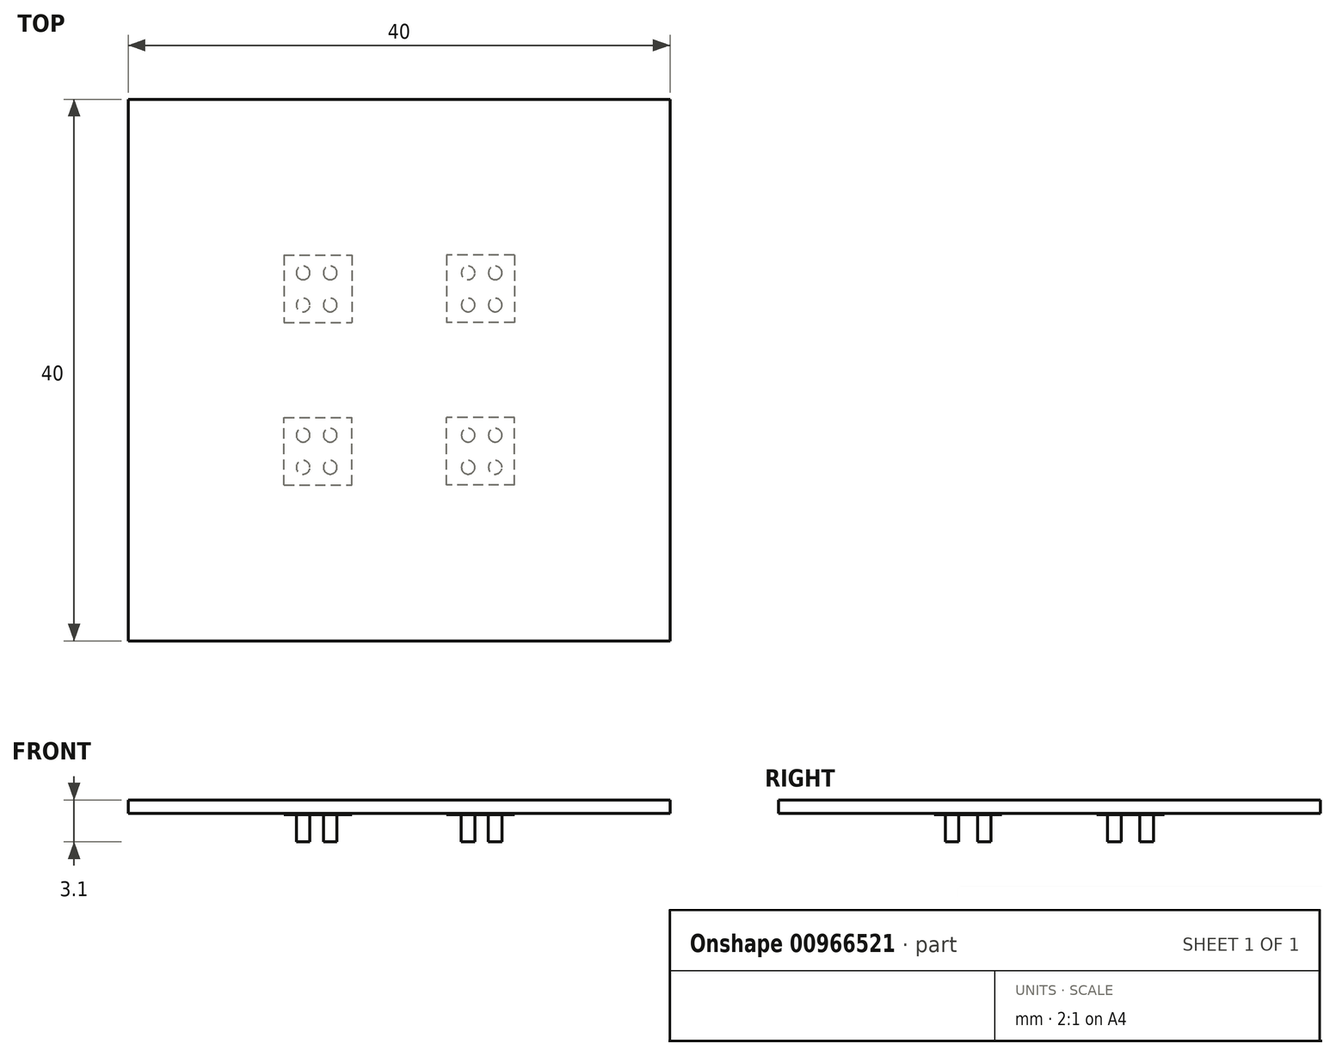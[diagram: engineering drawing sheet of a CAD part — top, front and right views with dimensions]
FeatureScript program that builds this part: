
annotation { "Feature Type Name" : "Feature", "Feature Type Description" : "" }
export const myFeature = defineFeature(function(context is Context, id is Id, definition is map)
    precondition{}
    {
        {
            var Q0;
            Q0=qCreatedBy(makeId("Top.planeOp"),FACE);
            var sketch = newSketch(context, id + "F0", { "sketchPlane" : qUnion([Q0])});
            skLineSegment(sketch, "E0.bottom", {"start": v(20, 20) * mm, "end": v(-20, 20) * mm});
            skLineSegment(sketch, "E0.top", {"start": v(20, -20) * mm, "end": v(-20, -20) * mm});
            skLineSegment(sketch, "E0.left", {"start": v(20, 20) * mm, "end": v(20, -20) * mm});
            skLineSegment(sketch, "E0.right", {"start": v(-20, 20) * mm, "end": v(-20, -20) * mm});
            skPoint(sketch, "E0.middle", {"position": v(0, 0) * mm});
            skLineSegment(sketch, "E1.bottom", {"start": v(-8.5, 8.5) * mm, "end": v(-3.5, 8.5) * mm});
            skLineSegment(sketch, "E1.top", {"start": v(-8.5, 3.5) * mm, "end": v(-3.5, 3.5) * mm});
            skLineSegment(sketch, "E1.left", {"start": v(-8.5, 8.5) * mm, "end": v(-8.5, 3.5) * mm});
            skLineSegment(sketch, "E1.right", {"start": v(-3.5, 8.5) * mm, "end": v(-3.5, 3.5) * mm});
            skLineSegment(sketch, "E2.MirrorCS", {"start": v(8.5, 8.5) * mm, "end": v(3.5, 8.5) * mm});
            skLineSegment(sketch, "E3.MirrorCS", {"start": v(8.5, 3.5) * mm, "end": v(3.5, 3.5) * mm});
            skLineSegment(sketch, "E4.MirrorCS", {"start": v(8.5, 8.5) * mm, "end": v(8.5, 3.5) * mm});
            skLineSegment(sketch, "E5.MirrorCS", {"start": v(3.5, 8.5) * mm, "end": v(3.5, 3.5) * mm});
            skLineSegment(sketch, "E6.MirrorCS", {"start": v(-8.5, -3.5) * mm, "end": v(-3.5, -3.5) * mm});
            skLineSegment(sketch, "E7.MirrorCS", {"start": v(-8.5, -8.5) * mm, "end": v(-3.5, -8.5) * mm});
            skLineSegment(sketch, "E8.MirrorCS", {"start": v(3.5, -8.5) * mm, "end": v(3.5, -3.5) * mm});
            skLineSegment(sketch, "E9.MirrorCS", {"start": v(-8.5, -8.5) * mm, "end": v(-8.5, -3.5) * mm});
            skLineSegment(sketch, "E10.MirrorCS", {"start": v(8.5, -8.5) * mm, "end": v(3.5, -8.5) * mm});
            skLineSegment(sketch, "E11.MirrorCS", {"start": v(8.5, -8.5) * mm, "end": v(8.5, -3.5) * mm});
            skLineSegment(sketch, "E12.MirrorCS", {"start": v(8.5, -3.5) * mm, "end": v(3.5, -3.5) * mm});
            skLineSegment(sketch, "E13.MirrorCS", {"start": v(-3.5, -8.5) * mm, "end": v(-3.5, -3.5) * mm});
            skSolve(sketch);
        }
        {
            var Q0;
            Q0=makeQuery(id+"F0.imprint","IMPRINT",FACE,{"disambiguationData":[TD([[makeQuery(id+"F0.imprint","IMPRINT",EDGE,{"derivedFrom":sQuery(id+"F0.wireOp",EDGE,"E1.bottom")}),-1.0]])]});
            var Q1;
            Q1=makeQuery(id+"F0.imprint","IMPRINT",FACE,{"disambiguationData":[TD([[makeQuery(id+"F0.imprint","IMPRINT",EDGE,{"derivedFrom":sQuery(id+"F0.wireOp",EDGE,"E2.MirrorCS")}),1.0]])]});
            var Q2;
            Q2=makeQuery(id+"F0.imprint","IMPRINT",FACE,{"disambiguationData":[TD([[makeQuery(id+"F0.imprint","IMPRINT",EDGE,{"derivedFrom":sQuery(id+"F0.wireOp",EDGE,"E8.MirrorCS")}),-1.0]])]});
            var Q3;
            Q3=makeQuery(id+"F0.imprint","IMPRINT",FACE,{"disambiguationData":[TD([[makeQuery(id+"F0.imprint","IMPRINT",EDGE,{"derivedFrom":sQuery(id+"F0.wireOp",EDGE,"E6.MirrorCS")}),-1.0]])]});
            extrude(context, id + "F1", {"entities" : qUnion([Q0, Q1, Q2, Q3]), "oppositeDirection" : true, "depth" : 0.1 * mm, "offsetDistance" : 25 * mm});
        }
        {
            var Q0;
            Q0=qCreatedBy(makeId("Top.planeOp"),FACE);
            var sketch = newSketch(context, id + "F2", { "sketchPlane" : qUnion([Q0])});
            skLineSegment(sketch, "E14.bottom", {"start": v(20, 20) * mm, "end": v(-20, 20) * mm});
            skLineSegment(sketch, "E14.top", {"start": v(20, -20) * mm, "end": v(-20, -20) * mm});
            skLineSegment(sketch, "E14.left", {"start": v(20, 20) * mm, "end": v(20, -20) * mm});
            skLineSegment(sketch, "E14.right", {"start": v(-20, 20) * mm, "end": v(-20, -20) * mm});
            skPoint(sketch, "E14.middle", {"position": v(0, 0) * mm});
            skSolve(sketch);
        }
        {
            var Q0;
            Q0 = qSketchRegion(id + "F2", true);
            extrude(context, id + "F3", {"entities" : qUnion([Q0]), "operationType" : NewBodyOperationType.ADD, "depth" : 1 * mm, "offsetDistance" : 25 * mm});
        }
        {
            var Q0;
            Q0=makeQuery(id+"F1.opExtrude","CAP_FACE",FACE,{"disambiguationData":[OSD([sQuery(id+"F0.wireOp",EDGE,"E6.MirrorCS"),sQuery(id+"F0.wireOp",EDGE,"E7.MirrorCS"),sQuery(id+"F0.wireOp",EDGE,"E9.MirrorCS"),sQuery(id+"F0.wireOp",EDGE,"E13.MirrorCS")])],"isStart":false});
            var sketch = newSketch(context, id + "F4", { "sketchPlane" : qUnion([Q0])});
            skCircle(sketch, "E15", {"center": v(-7.1, 7.18) * mm, "radius": 0.5 * mm});
            skCircle(sketch, "E16.1.0.0", {"center": v(-5.1, 7.18) * mm, "radius": 0.5 * mm});
            skLineSegment(sketch, "E16.direction1", {"start": v(-7.1, 7.18) * mm, "end": v(-5.1, 7.18) * mm, "construction": true});
            skCircle(sketch, "E17", {"center": v(-7.1, 4.8) * mm, "radius": 0.5 * mm});
            skCircle(sketch, "E18.1.0.0", {"center": v(-5.1, 4.8) * mm, "radius": 0.5 * mm});
            skLineSegment(sketch, "E18.direction1", {"start": v(-7.1, 4.8) * mm, "end": v(-5.1, 4.8) * mm, "construction": true});
            skCircle(sketch, "E19.MirrorC", {"center": v(7.1, 7.18) * mm, "radius": 0.5 * mm});
            skCircle(sketch, "E20.MirrorC", {"center": v(5.1, 7.18) * mm, "radius": 0.5 * mm});
            skCircle(sketch, "E21.MirrorC", {"center": v(5.1, 4.8) * mm, "radius": 0.5 * mm});
            skCircle(sketch, "E22.MirrorC", {"center": v(7.1, 4.8) * mm, "radius": 0.5 * mm});
            skCircle(sketch, "E23.MirrorC", {"center": v(-7.1, -4.8) * mm, "radius": 0.5 * mm});
            skCircle(sketch, "E24.MirrorC", {"center": v(-5.1, -7.18) * mm, "radius": 0.5 * mm});
            skCircle(sketch, "E25.MirrorC", {"center": v(-7.1, -7.18) * mm, "radius": 0.5 * mm});
            skCircle(sketch, "E26.MirrorC", {"center": v(-5.1, -4.8) * mm, "radius": 0.5 * mm});
            skCircle(sketch, "E27.MirrorC", {"center": v(5.1, -7.18) * mm, "radius": 0.5 * mm});
            skCircle(sketch, "E28.MirrorC", {"center": v(5.1, -4.8) * mm, "radius": 0.5 * mm});
            skCircle(sketch, "E29.MirrorC", {"center": v(7.1, -4.8) * mm, "radius": 0.5 * mm});
            skCircle(sketch, "E30.MirrorC", {"center": v(7.1, -7.18) * mm, "radius": 0.5 * mm});
            skSolve(sketch);
        }
        {
            var Q0;
            Q0 = qSketchRegion(id + "F4", true);
            extrude(context, id + "F5", {"entities" : qUnion([Q0]), "operationType" : NewBodyOperationType.ADD, "depth" : 2 * mm, "offsetDistance" : 25 * mm});
        }
    });
